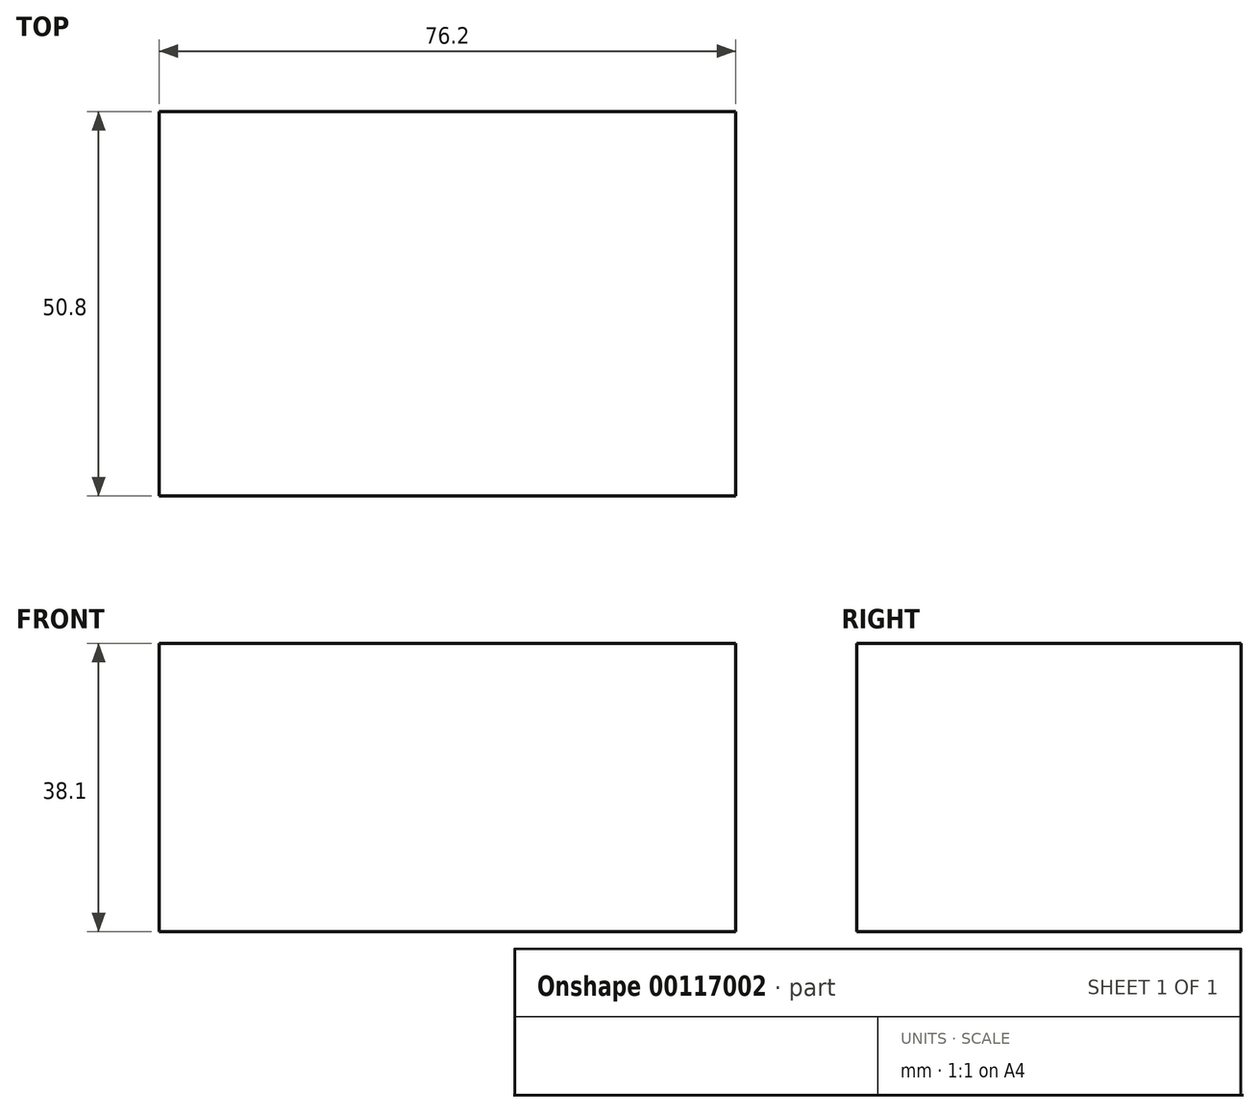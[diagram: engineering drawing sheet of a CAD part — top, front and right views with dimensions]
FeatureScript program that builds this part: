
annotation { "Feature Type Name" : "Feature", "Feature Type Description" : "" }
export const myFeature = defineFeature(function(context is Context, id is Id, definition is map)
    precondition{}
    {
        {
            var Q0;
            Q0=qCreatedBy(makeId("Front.planeOp"),FACE);
            var sketch = newSketch(context, id + "F0", { "sketchPlane" : qUnion([Q0])});
            skLineSegment(sketch, "E0.bottom", {"start": v(-34.14, 11.95) * mm, "end": v(42.06, 11.95) * mm});
            skLineSegment(sketch, "E0.top", {"start": v(-34.14, -26.15) * mm, "end": v(42.06, -26.15) * mm});
            skLineSegment(sketch, "E0.left", {"start": v(-34.14, 11.95) * mm, "end": v(-34.14, -26.15) * mm});
            skLineSegment(sketch, "E0.right", {"start": v(42.06, 11.95) * mm, "end": v(42.06, -26.15) * mm});
            skSolve(sketch);
        }
        {
            var Q0;
            Q0 = qSketchRegion(id + "F0", true);
            extrude(context, id + "F1", {"entities" : qUnion([Q0]), "oppositeDirection" : true, "depth" : 50.8 * mm});
        }
    });
